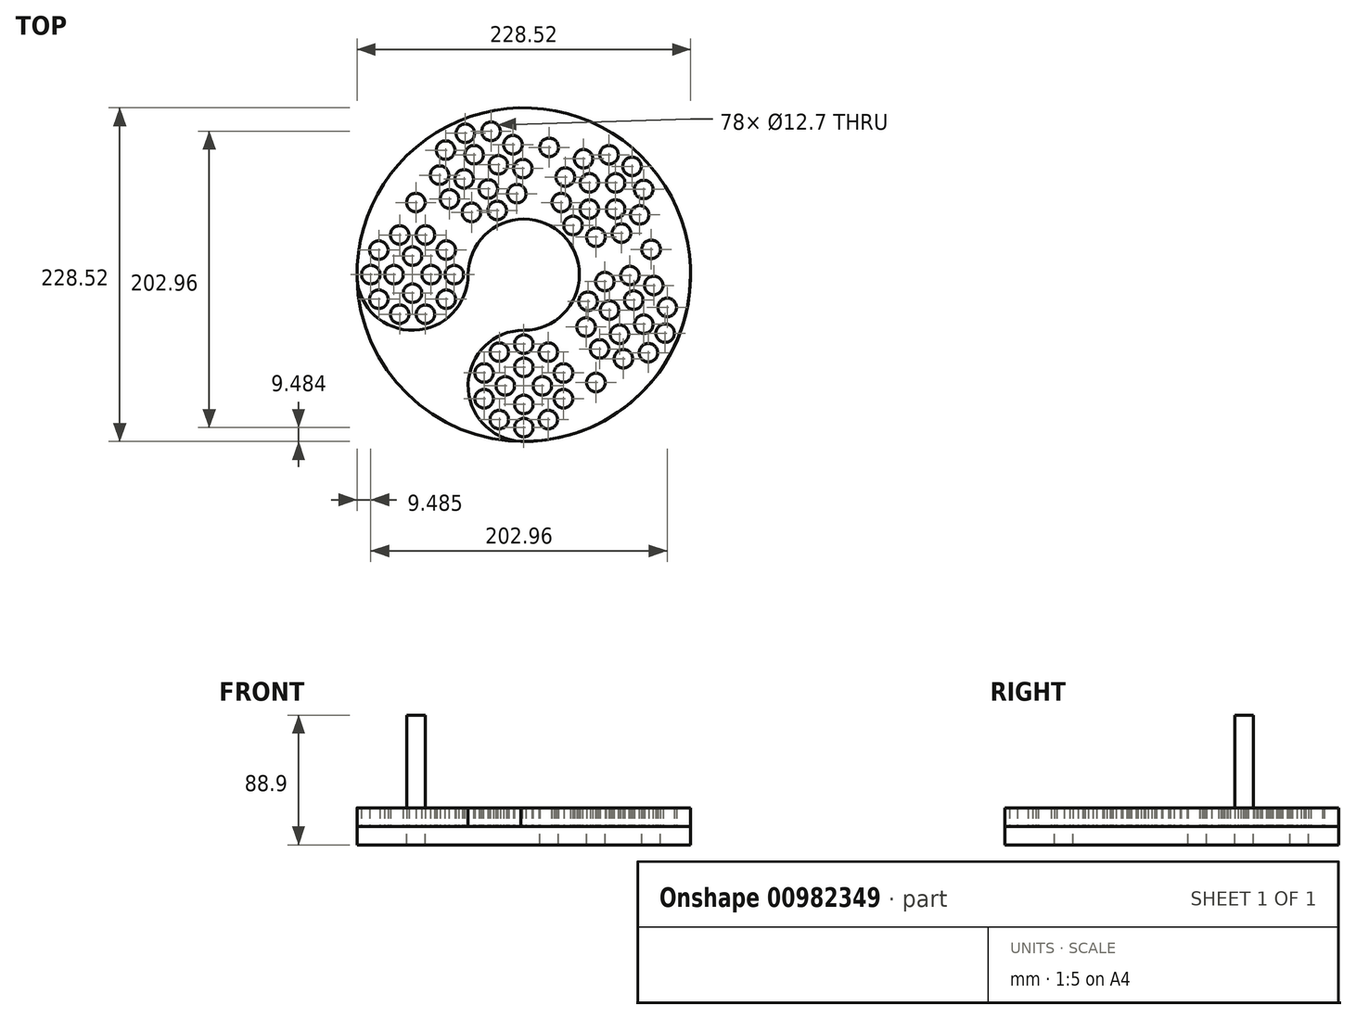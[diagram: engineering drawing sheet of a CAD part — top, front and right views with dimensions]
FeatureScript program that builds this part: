
annotation { "Feature Type Name" : "Feature", "Feature Type Description" : "" }
export const myFeature = defineFeature(function(context is Context, id is Id, definition is map)
    precondition{}
    {
        {
            var Q0;
            Q0=qCreatedBy(makeId("Top.planeOp"),FACE);
            var sketch = newSketch(context, id + "F0", { "sketchPlane" : qUnion([Q0])});
            skArc(sketch, "E0", {"start": v(-101.16, 18.78) * mm, "mid": v(-64.22, -21.5) * mm, "end": v(-25.02, 16.59) * mm});
            skCircle(sketch, "E1", {"center": v(13.08, 16.59) * mm, "radius": 38.1 * mm});
            skArc(sketch, "E2", {"start": v(-63.12, 16.59) * mm, "mid": v(66.96, 70.47) * mm, "end": v(13.08, -59.61) * mm, "construction": true});
            skArc(sketch, "E3", {"start": v(13.08, -21.51) * mm, "mid": v(-25, -60.7) * mm, "end": v(15.27, -97.65) * mm});
            skArc(sketch, "E4", {"start": v(-101.16, 14.4) * mm, "mid": v(92.3, 98.92) * mm, "end": v(15.27, -97.65) * mm});
            skCircle(sketch, "E5", {"center": v(13.08, 16.59) * mm, "radius": 114.26 * mm});
            skCircle(sketch, "E6", {"center": v(-50.42, 16.59) * mm, "radius": 6.35 * mm});
            skCircle(sketch, "E7", {"center": v(-34.55, 16.59) * mm, "radius": 6.35 * mm});
            skCircle(sketch, "E8.1.0", {"center": v(-63.12, 29.29) * mm, "radius": 6.35 * mm});
            skCircle(sketch, "E8.2.0", {"center": v(-75.82, 16.59) * mm, "radius": 6.35 * mm});
            skCircle(sketch, "E8.3.0", {"center": v(-63.12, 3.89) * mm, "radius": 6.35 * mm});
            skCircle(sketch, "E9.1.0", {"center": v(-40, 33.38) * mm, "radius": 6.35 * mm});
            skCircle(sketch, "E9.2.0", {"center": v(-54.3, 43.77) * mm, "radius": 6.35 * mm});
            skCircle(sketch, "E9.3.0", {"center": v(-71.95, 43.77) * mm, "radius": 6.35 * mm});
            skCircle(sketch, "E9.4.0", {"center": v(-86.24, 33.38) * mm, "radius": 6.35 * mm});
            skCircle(sketch, "E9.5.0", {"center": v(-91.7, 16.59) * mm, "radius": 6.35 * mm});
            skCircle(sketch, "E9.6.0", {"center": v(-86.24, -0.2) * mm, "radius": 6.35 * mm});
            skCircle(sketch, "E9.7.0", {"center": v(-71.95, -10.59) * mm, "radius": 6.35 * mm});
            skCircle(sketch, "E9.8.0", {"center": v(-54.3, -10.59) * mm, "radius": 6.35 * mm});
            skCircle(sketch, "E9.9.0", {"center": v(-40, -0.2) * mm, "radius": 6.35 * mm});
            skLineSegment(sketch, "E10", {"start": v(-63.12, 16.59) * mm, "end": v(13.08, 16.59) * mm, "construction": true});
            skLineSegment(sketch, "E11", {"start": v(13.08, 16.59) * mm, "end": v(13.08, -59.61) * mm, "construction": true});
            skCircle(sketch, "E12.1.0", {"center": v(5.65, 105.55) * mm, "radius": 6.35 * mm});
            skCircle(sketch, "E12.1.1", {"center": v(-9.41, 114.77) * mm, "radius": 6.35 * mm});
            skCircle(sketch, "E12.1.2", {"center": v(-27.02, 113.39) * mm, "radius": 6.35 * mm});
            skCircle(sketch, "E12.1.3", {"center": v(-20.94, 98.72) * mm, "radius": 6.35 * mm});
            skCircle(sketch, "E12.1.4", {"center": v(-40.45, 101.92) * mm, "radius": 6.35 * mm});
            skCircle(sketch, "E12.1.5", {"center": v(-44.57, 84.75) * mm, "radius": 6.35 * mm});
            skCircle(sketch, "E12.1.6", {"center": v(-27.81, 82.13) * mm, "radius": 6.35 * mm});
            skCircle(sketch, "E12.1.7", {"center": v(-37.8, 68.43) * mm, "radius": 6.35 * mm});
            skCircle(sketch, "E12.1.8", {"center": v(-22.75, 59.2) * mm, "radius": 6.35 * mm});
            skCircle(sketch, "E12.1.9", {"center": v(-5.15, 60.59) * mm, "radius": 6.35 * mm});
            skCircle(sketch, "E12.1.10", {"center": v(-11.22, 75.26) * mm, "radius": 6.35 * mm});
            skCircle(sketch, "E12.1.11", {"center": v(-4.35, 91.85) * mm, "radius": 6.35 * mm});
            skCircle(sketch, "E12.1.12", {"center": v(12.4, 89.23) * mm, "radius": 6.35 * mm});
            skCircle(sketch, "E12.1.13", {"center": v(8.28, 72.06) * mm, "radius": 6.35 * mm});
            skCircle(sketch, "E12.2.0", {"center": v(92.42, 57.5) * mm, "radius": 6.35 * mm});
            skCircle(sketch, "E12.2.1", {"center": v(95.18, 74.94) * mm, "radius": 6.35 * mm});
            skCircle(sketch, "E12.2.2", {"center": v(87.17, 90.68) * mm, "radius": 6.35 * mm});
            skCircle(sketch, "E12.2.3", {"center": v(75.94, 79.45) * mm, "radius": 6.35 * mm});
            skCircle(sketch, "E12.2.4", {"center": v(71.43, 98.7) * mm, "radius": 6.35 * mm});
            skCircle(sketch, "E12.2.5", {"center": v(53.99, 95.93) * mm, "radius": 6.35 * mm});
            skCircle(sketch, "E12.2.6", {"center": v(57.98, 79.45) * mm, "radius": 6.35 * mm});
            skCircle(sketch, "E12.2.7", {"center": v(41.5, 83.44) * mm, "radius": 6.35 * mm});
            skCircle(sketch, "E12.2.8", {"center": v(38.74, 66) * mm, "radius": 6.35 * mm});
            skCircle(sketch, "E12.2.9", {"center": v(46.76, 50.26) * mm, "radius": 6.35 * mm});
            skCircle(sketch, "E12.2.10", {"center": v(57.98, 61.5) * mm, "radius": 6.35 * mm});
            skCircle(sketch, "E12.2.11", {"center": v(75.94, 61.5) * mm, "radius": 6.35 * mm});
            skCircle(sketch, "E12.2.12", {"center": v(79.93, 45.01) * mm, "radius": 6.35 * mm});
            skCircle(sketch, "E12.2.13", {"center": v(62.5, 42.25) * mm, "radius": 6.35 * mm});
            skCircle(sketch, "E12.3.0", {"center": v(81.24, -41.06) * mm, "radius": 6.35 * mm});
            skCircle(sketch, "E12.3.1", {"center": v(98.4, -36.94) * mm, "radius": 6.35 * mm});
            skCircle(sketch, "E12.3.2", {"center": v(109.88, -23.5) * mm, "radius": 6.35 * mm});
            skCircle(sketch, "E12.3.3", {"center": v(95.21, -17.43) * mm, "radius": 6.35 * mm});
            skCircle(sketch, "E12.3.4", {"center": v(111.26, -5.9) * mm, "radius": 6.35 * mm});
            skCircle(sketch, "E12.3.5", {"center": v(102.04, 9.16) * mm, "radius": 6.35 * mm});
            skCircle(sketch, "E12.3.6", {"center": v(88.34, -0.84) * mm, "radius": 6.35 * mm});
            skCircle(sketch, "E12.3.7", {"center": v(85.72, 15.92) * mm, "radius": 6.35 * mm});
            skCircle(sketch, "E12.3.8", {"center": v(68.55, 11.8) * mm, "radius": 6.35 * mm});
            skCircle(sketch, "E12.3.9", {"center": v(57.08, -1.64) * mm, "radius": 6.35 * mm});
            skCircle(sketch, "E12.3.10", {"center": v(71.75, -7.71) * mm, "radius": 6.35 * mm});
            skCircle(sketch, "E12.3.11", {"center": v(78.62, -24.3) * mm, "radius": 6.35 * mm});
            skCircle(sketch, "E12.3.12", {"center": v(64.92, -34.3) * mm, "radius": 6.35 * mm});
            skCircle(sketch, "E12.3.13", {"center": v(55.7, -19.24) * mm, "radius": 6.35 * mm});
            skCircle(sketch, "E12.4.0", {"center": v(-14.1, -68.44) * mm, "radius": 6.35 * mm});
            skCircle(sketch, "E12.4.1", {"center": v(-3.72, -82.73) * mm, "radius": 6.35 * mm});
            skCircle(sketch, "E12.4.2", {"center": v(13.08, -88.19) * mm, "radius": 6.35 * mm});
            skCircle(sketch, "E12.4.3", {"center": v(13.08, -72.31) * mm, "radius": 6.35 * mm});
            skCircle(sketch, "E12.4.4", {"center": v(29.88, -82.73) * mm, "radius": 6.35 * mm});
            skCircle(sketch, "E12.4.5", {"center": v(40.26, -68.44) * mm, "radius": 6.35 * mm});
            skCircle(sketch, "E12.4.6", {"center": v(25.78, -59.61) * mm, "radius": 6.35 * mm});
            skCircle(sketch, "E12.4.7", {"center": v(40.26, -50.78) * mm, "radius": 6.35 * mm});
            skCircle(sketch, "E12.4.8", {"center": v(29.88, -36.5) * mm, "radius": 6.35 * mm});
            skCircle(sketch, "E12.4.9", {"center": v(13.08, -31.04) * mm, "radius": 6.35 * mm});
            skCircle(sketch, "E12.4.10", {"center": v(13.08, -46.91) * mm, "radius": 6.35 * mm});
            skCircle(sketch, "E12.4.11", {"center": v(0.38, -59.61) * mm, "radius": 6.35 * mm});
            skCircle(sketch, "E12.4.12", {"center": v(-14.1, -50.78) * mm, "radius": 6.35 * mm});
            skCircle(sketch, "E12.4.13", {"center": v(-3.72, -36.5) * mm, "radius": 6.35 * mm});
            skLineSegment(sketch, "E12.anchor1", {"start": v(13.08, 16.59) * mm, "end": v(-91.7, 16.59) * mm, "construction": true});
            skLineSegment(sketch, "E12.anchor2", {"start": v(13.08, 16.59) * mm, "end": v(13.08, -88.19) * mm, "construction": true});
            skCircle(sketch, "E13.1.0", {"center": v(-60.84, 65.98) * mm, "radius": 6.35 * mm});
            skCircle(sketch, "E13.3.0", {"center": v(30.42, 103.78) * mm, "radius": 6.35 * mm});
            skCircle(sketch, "E13.5.0", {"center": v(100.27, 33.93) * mm, "radius": 6.35 * mm});
            skCircle(sketch, "E13.7.0", {"center": v(62.47, -57.33) * mm, "radius": 6.35 * mm});
            skLineSegment(sketch, "E13.anchor1", {"start": v(13.08, 16.59) * mm, "end": v(-75.82, 16.59) * mm, "construction": true});
            skLineSegment(sketch, "E13.anchor2", {"start": v(13.08, 16.59) * mm, "end": v(13.08, -72.31) * mm, "construction": true});
            skSolve(sketch);
        }
        {
            var Q0;
            {var subQ0=sQuery(id+"F0.wireOp",EDGE,"E1");var subQ1=sQuery(id+"F0.wireOp",EDGE,"E0");var subQ2=makeQuery(id+"F0.imprint","INTERSECT",VERTEX,{"derivedFrom":[subQ1,subQ0]});Q0=makeQuery(id+"F0.imprint","IMPRINT",FACE,{"disambiguationData":[TD([[makeQuery(id+"F0.imprint","IMPRINT",EDGE,{"disambiguationData":[TD([[subQ2,1.0]])],"derivedFrom":subQ1}),-1.0]])]});}
            var Q1;
            {var subQ0=sQuery(id+"F0.wireOp",EDGE,"E1");var subQ1=makeQuery(id+"F0.imprint","INTERSECT",VERTEX,{"derivedFrom":[sQuery(id+"F0.wireOp",EDGE,"E0"),subQ0]});Q1=makeQuery(id+"F0.imprint","IMPRINT",FACE,{"disambiguationData":[TD([[makeQuery(id+"F0.imprint","IMPRINT",EDGE,{"disambiguationData":[TD([[subQ1,-1.0]])],"derivedFrom":subQ0}),1.0]])]});}
            var Q2;
            Q2=makeQuery(id+"F0.imprint","IMPRINT",FACE,{"disambiguationData":[TD([[makeQuery(id+"F0.imprint","IMPRINT",EDGE,{"derivedFrom":sQuery(id+"F0.wireOp",EDGE,"E6")}),-1.0]])]});
            var Q3;
            Q3=makeQuery(id+"F0.imprint","IMPRINT",FACE,{"disambiguationData":[TD([[makeQuery(id+"F0.imprint","IMPRINT",EDGE,{"derivedFrom":sQuery(id+"F0.wireOp",EDGE,"E9.4.0")}),1.0]])]});
            var Q4;
            Q4=makeQuery(id+"F0.imprint","IMPRINT",FACE,{"disambiguationData":[TD([[makeQuery(id+"F0.imprint","IMPRINT",EDGE,{"derivedFrom":sQuery(id+"F0.wireOp",EDGE,"E12.4.12")}),1.0]])]});
            var Q5;
            Q5=makeQuery(id+"F0.imprint","IMPRINT",FACE,{"disambiguationData":[TD([[makeQuery(id+"F0.imprint","IMPRINT",EDGE,{"derivedFrom":sQuery(id+"F0.wireOp",EDGE,"E12.4.10")}),1.0]])]});
            var Q6;
            Q6=makeQuery(id+"F0.imprint","IMPRINT",FACE,{"disambiguationData":[TD([[makeQuery(id+"F0.imprint","IMPRINT",EDGE,{"derivedFrom":sQuery(id+"F0.wireOp",EDGE,"E12.4.2")}),1.0]])]});
            var Q7;
            Q7=makeQuery(id+"F0.imprint","IMPRINT",FACE,{"disambiguationData":[TD([[makeQuery(id+"F0.imprint","IMPRINT",EDGE,{"derivedFrom":sQuery(id+"F0.wireOp",EDGE,"E9.3.0")}),1.0]])]});
            var Q8;
            Q8=makeQuery(id+"F0.imprint","IMPRINT",FACE,{"disambiguationData":[TD([[makeQuery(id+"F0.imprint","IMPRINT",EDGE,{"derivedFrom":sQuery(id+"F0.wireOp",EDGE,"E12.4.13")}),1.0]])]});
            var Q9;
            Q9=makeQuery(id+"F0.imprint","IMPRINT",FACE,{"disambiguationData":[TD([[makeQuery(id+"F0.imprint","IMPRINT",EDGE,{"derivedFrom":sQuery(id+"F0.wireOp",EDGE,"E12.4.8")}),1.0]])]});
            var Q10;
            Q10=makeQuery(id+"F0.imprint","IMPRINT",FACE,{"disambiguationData":[TD([[makeQuery(id+"F0.imprint","IMPRINT",EDGE,{"derivedFrom":sQuery(id+"F0.wireOp",EDGE,"E12.4.3")}),1.0]])]});
            var Q11;
            Q11=makeQuery(id+"F0.imprint","IMPRINT",FACE,{"disambiguationData":[TD([[makeQuery(id+"F0.imprint","IMPRINT",EDGE,{"derivedFrom":sQuery(id+"F0.wireOp",EDGE,"E12.3.12")}),1.0]])]});
            var Q12;
            Q12=makeQuery(id+"F0.imprint","IMPRINT",FACE,{"disambiguationData":[TD([[makeQuery(id+"F0.imprint","IMPRINT",EDGE,{"derivedFrom":sQuery(id+"F0.wireOp",EDGE,"E12.4.0")}),1.0]])]});
            var Q13;
            Q13=makeQuery(id+"F0.imprint","IMPRINT",FACE,{"disambiguationData":[TD([[makeQuery(id+"F0.imprint","IMPRINT",EDGE,{"derivedFrom":sQuery(id+"F0.wireOp",EDGE,"E12.4.1")}),1.0]])]});
            var Q14;
            Q14=makeQuery(id+"F0.imprint","IMPRINT",FACE,{"disambiguationData":[TD([[makeQuery(id+"F0.imprint","IMPRINT",EDGE,{"derivedFrom":sQuery(id+"F0.wireOp",EDGE,"E12.4.9")}),1.0]])]});
            var Q15;
            Q15=makeQuery(id+"F0.imprint","IMPRINT",FACE,{"disambiguationData":[TD([[makeQuery(id+"F0.imprint","IMPRINT",EDGE,{"derivedFrom":sQuery(id+"F0.wireOp",EDGE,"E12.3.10")}),1.0]])]});
            var Q16;
            Q16=makeQuery(id+"F0.imprint","IMPRINT",FACE,{"disambiguationData":[TD([[makeQuery(id+"F0.imprint","IMPRINT",EDGE,{"derivedFrom":sQuery(id+"F0.wireOp",EDGE,"E8.2.0")}),1.0]])]});
            var Q17;
            Q17=makeQuery(id+"F0.imprint","IMPRINT",FACE,{"disambiguationData":[TD([[makeQuery(id+"F0.imprint","IMPRINT",EDGE,{"derivedFrom":sQuery(id+"F0.wireOp",EDGE,"E12.4.5")}),1.0]])]});
            var Q18;
            Q18=makeQuery(id+"F0.imprint","IMPRINT",FACE,{"disambiguationData":[TD([[makeQuery(id+"F0.imprint","IMPRINT",EDGE,{"derivedFrom":sQuery(id+"F0.wireOp",EDGE,"E12.3.4")}),1.0]])]});
            var Q19;
            Q19=makeQuery(id+"F0.imprint","IMPRINT",FACE,{"disambiguationData":[TD([[makeQuery(id+"F0.imprint","IMPRINT",EDGE,{"derivedFrom":sQuery(id+"F0.wireOp",EDGE,"E12.3.13")}),1.0]])]});
            var Q20;
            Q20=makeQuery(id+"F0.imprint","IMPRINT",FACE,{"disambiguationData":[TD([[makeQuery(id+"F0.imprint","IMPRINT",EDGE,{"derivedFrom":sQuery(id+"F0.wireOp",EDGE,"E9.6.0")}),1.0]])]});
            var Q21;
            Q21=makeQuery(id+"F0.imprint","IMPRINT",FACE,{"disambiguationData":[TD([[makeQuery(id+"F0.imprint","IMPRINT",EDGE,{"derivedFrom":sQuery(id+"F0.wireOp",EDGE,"E12.3.7")}),1.0]])]});
            var Q22;
            Q22=makeQuery(id+"F0.imprint","IMPRINT",FACE,{"disambiguationData":[TD([[makeQuery(id+"F0.imprint","IMPRINT",EDGE,{"derivedFrom":sQuery(id+"F0.wireOp",EDGE,"E9.9.0")}),1.0]])]});
            var Q23;
            Q23=makeQuery(id+"F0.imprint","IMPRINT",FACE,{"disambiguationData":[TD([[makeQuery(id+"F0.imprint","IMPRINT",EDGE,{"derivedFrom":sQuery(id+"F0.wireOp",EDGE,"E12.3.3")}),1.0]])]});
            var Q24;
            Q24=makeQuery(id+"F0.imprint","IMPRINT",FACE,{"disambiguationData":[TD([[makeQuery(id+"F0.imprint","IMPRINT",EDGE,{"derivedFrom":sQuery(id+"F0.wireOp",EDGE,"E12.3.2")}),1.0]])]});
            var Q25;
            Q25=makeQuery(id+"F0.imprint","IMPRINT",FACE,{"disambiguationData":[TD([[makeQuery(id+"F0.imprint","IMPRINT",EDGE,{"derivedFrom":sQuery(id+"F0.wireOp",EDGE,"E12.3.1")}),1.0]])]});
            var Q26;
            Q26=makeQuery(id+"F0.imprint","IMPRINT",FACE,{"disambiguationData":[TD([[makeQuery(id+"F0.imprint","IMPRINT",EDGE,{"derivedFrom":sQuery(id+"F0.wireOp",EDGE,"E9.5.0")}),1.0]])]});
            var Q27;
            Q27=makeQuery(id+"F0.imprint","IMPRINT",FACE,{"disambiguationData":[TD([[makeQuery(id+"F0.imprint","IMPRINT",EDGE,{"derivedFrom":sQuery(id+"F0.wireOp",EDGE,"E12.4.4")}),1.0]])]});
            var Q28;
            Q28=makeQuery(id+"F0.imprint","IMPRINT",FACE,{"disambiguationData":[TD([[makeQuery(id+"F0.imprint","IMPRINT",EDGE,{"derivedFrom":sQuery(id+"F0.wireOp",EDGE,"E12.3.0")}),1.0]])]});
            var Q29;
            Q29=makeQuery(id+"F0.imprint","IMPRINT",FACE,{"disambiguationData":[TD([[makeQuery(id+"F0.imprint","IMPRINT",EDGE,{"derivedFrom":sQuery(id+"F0.wireOp",EDGE,"E12.4.11")}),1.0]])]});
            var Q30;
            Q30=makeQuery(id+"F0.imprint","IMPRINT",FACE,{"disambiguationData":[TD([[makeQuery(id+"F0.imprint","IMPRINT",EDGE,{"derivedFrom":sQuery(id+"F0.wireOp",EDGE,"E12.2.0")}),1.0]])]});
            var Q31;
            Q31=makeQuery(id+"F0.imprint","IMPRINT",FACE,{"disambiguationData":[TD([[makeQuery(id+"F0.imprint","IMPRINT",EDGE,{"derivedFrom":sQuery(id+"F0.wireOp",EDGE,"E12.2.1")}),1.0]])]});
            var Q32;
            Q32=makeQuery(id+"F0.imprint","IMPRINT",FACE,{"disambiguationData":[TD([[makeQuery(id+"F0.imprint","IMPRINT",EDGE,{"derivedFrom":sQuery(id+"F0.wireOp",EDGE,"E8.3.0")}),1.0]])]});
            var Q33;
            Q33=makeQuery(id+"F0.imprint","IMPRINT",FACE,{"disambiguationData":[TD([[makeQuery(id+"F0.imprint","IMPRINT",EDGE,{"derivedFrom":sQuery(id+"F0.wireOp",EDGE,"E12.3.9")}),1.0]])]});
            var Q34;
            Q34=makeQuery(id+"F0.imprint","IMPRINT",FACE,{"disambiguationData":[TD([[makeQuery(id+"F0.imprint","IMPRINT",EDGE,{"derivedFrom":sQuery(id+"F0.wireOp",EDGE,"E12.3.5")}),1.0]])]});
            var Q35;
            {var subQ0=sQuery(id+"F0.wireOp",EDGE,"E5");var subQ1=sQuery(id+"F0.wireOp",EDGE,"E3");var subQ2=makeQuery(id+"F0.imprint","INTERSECT",VERTEX,{"disambiguationData":[OD(0.0)],"derivedFrom":[subQ1,subQ0]});Q35=makeQuery(id+"F0.imprint","IMPRINT",FACE,{"disambiguationData":[TD([[makeQuery(id+"F0.imprint","IMPRINT",EDGE,{"disambiguationData":[TD([[subQ2,1.0]])],"derivedFrom":subQ1}),1.0]])]});}
            var Q36;
            Q36=makeQuery(id+"F0.imprint","IMPRINT",FACE,{"disambiguationData":[TD([[makeQuery(id+"F0.imprint","IMPRINT",EDGE,{"derivedFrom":sQuery(id+"F0.wireOp",EDGE,"E12.4.6")}),1.0]])]});
            var Q37;
            Q37=makeQuery(id+"F0.imprint","IMPRINT",FACE,{"disambiguationData":[TD([[makeQuery(id+"F0.imprint","IMPRINT",EDGE,{"derivedFrom":sQuery(id+"F0.wireOp",EDGE,"E12.3.11")}),1.0]])]});
            var Q38;
            Q38=makeQuery(id+"F0.imprint","IMPRINT",FACE,{"disambiguationData":[TD([[makeQuery(id+"F0.imprint","IMPRINT",EDGE,{"derivedFrom":sQuery(id+"F0.wireOp",EDGE,"E12.3.6")}),1.0]])]});
            var Q39;
            Q39=makeQuery(id+"F0.imprint","IMPRINT",FACE,{"disambiguationData":[TD([[makeQuery(id+"F0.imprint","IMPRINT",EDGE,{"derivedFrom":sQuery(id+"F0.wireOp",EDGE,"E9.7.0")}),1.0]])]});
            var Q40;
            Q40=makeQuery(id+"F0.imprint","IMPRINT",FACE,{"disambiguationData":[TD([[makeQuery(id+"F0.imprint","IMPRINT",EDGE,{"derivedFrom":sQuery(id+"F0.wireOp",EDGE,"E12.4.7")}),1.0]])]});
            var Q41;
            Q41=makeQuery(id+"F0.imprint","IMPRINT",FACE,{"disambiguationData":[TD([[makeQuery(id+"F0.imprint","IMPRINT",EDGE,{"derivedFrom":sQuery(id+"F0.wireOp",EDGE,"E9.8.0")}),1.0]])]});
            var Q42;
            Q42=makeQuery(id+"F0.imprint","IMPRINT",FACE,{"disambiguationData":[TD([[makeQuery(id+"F0.imprint","IMPRINT",EDGE,{"derivedFrom":sQuery(id+"F0.wireOp",EDGE,"E12.2.12")}),1.0]])]});
            var Q43;
            Q43=makeQuery(id+"F0.imprint","IMPRINT",FACE,{"disambiguationData":[TD([[makeQuery(id+"F0.imprint","IMPRINT",EDGE,{"derivedFrom":sQuery(id+"F0.wireOp",EDGE,"E12.1.4")}),1.0]])]});
            var Q44;
            Q44=makeQuery(id+"F0.imprint","IMPRINT",FACE,{"disambiguationData":[TD([[makeQuery(id+"F0.imprint","IMPRINT",EDGE,{"derivedFrom":sQuery(id+"F0.wireOp",EDGE,"E12.2.3")}),1.0]])]});
            var Q45;
            Q45=makeQuery(id+"F0.imprint","IMPRINT",FACE,{"disambiguationData":[TD([[makeQuery(id+"F0.imprint","IMPRINT",EDGE,{"derivedFrom":sQuery(id+"F0.wireOp",EDGE,"E12.2.5")}),1.0]])]});
            var Q46;
            Q46=makeQuery(id+"F0.imprint","IMPRINT",FACE,{"disambiguationData":[TD([[makeQuery(id+"F0.imprint","IMPRINT",EDGE,{"derivedFrom":sQuery(id+"F0.wireOp",EDGE,"E6")}),1.0]])]});
            var Q47;
            Q47=makeQuery(id+"F0.imprint","IMPRINT",FACE,{"disambiguationData":[TD([[makeQuery(id+"F0.imprint","IMPRINT",EDGE,{"derivedFrom":sQuery(id+"F0.wireOp",EDGE,"E12.1.9")}),1.0]])]});
            var Q48;
            Q48=makeQuery(id+"F0.imprint","IMPRINT",FACE,{"disambiguationData":[TD([[makeQuery(id+"F0.imprint","IMPRINT",EDGE,{"derivedFrom":sQuery(id+"F0.wireOp",EDGE,"E12.2.4")}),1.0]])]});
            var Q49;
            {var subQ0=sQuery(id+"F0.wireOp",EDGE,"E5");var subQ1=sQuery(id+"F0.wireOp",EDGE,"E0");var subQ2=makeQuery(id+"F0.imprint","INTERSECT",VERTEX,{"disambiguationData":[OD(0.0)],"derivedFrom":[subQ1,subQ0]});Q49=makeQuery(id+"F0.imprint","IMPRINT",FACE,{"disambiguationData":[TD([[makeQuery(id+"F0.imprint","IMPRINT",EDGE,{"disambiguationData":[TD([[subQ2,-1.0]])],"derivedFrom":subQ1}),1.0]])]});}
            var Q50;
            Q50=makeQuery(id+"F0.imprint","IMPRINT",FACE,{"disambiguationData":[TD([[makeQuery(id+"F0.imprint","IMPRINT",EDGE,{"derivedFrom":sQuery(id+"F0.wireOp",EDGE,"E9.2.0")}),1.0]])]});
            var Q51;
            Q51=makeQuery(id+"F0.imprint","IMPRINT",FACE,{"disambiguationData":[TD([[makeQuery(id+"F0.imprint","IMPRINT",EDGE,{"derivedFrom":sQuery(id+"F0.wireOp",EDGE,"E12.1.10")}),1.0]])]});
            var Q52;
            Q52=makeQuery(id+"F0.imprint","IMPRINT",FACE,{"disambiguationData":[TD([[makeQuery(id+"F0.imprint","IMPRINT",EDGE,{"derivedFrom":sQuery(id+"F0.wireOp",EDGE,"E12.2.6")}),1.0]])]});
            var Q53;
            Q53=makeQuery(id+"F0.imprint","IMPRINT",FACE,{"disambiguationData":[TD([[makeQuery(id+"F0.imprint","IMPRINT",EDGE,{"derivedFrom":sQuery(id+"F0.wireOp",EDGE,"E12.1.0")}),1.0]])]});
            var Q54;
            Q54=makeQuery(id+"F0.imprint","IMPRINT",FACE,{"disambiguationData":[TD([[makeQuery(id+"F0.imprint","IMPRINT",EDGE,{"derivedFrom":sQuery(id+"F0.wireOp",EDGE,"E12.1.13")}),1.0]])]});
            var Q55;
            Q55=makeQuery(id+"F0.imprint","IMPRINT",FACE,{"disambiguationData":[TD([[makeQuery(id+"F0.imprint","IMPRINT",EDGE,{"derivedFrom":sQuery(id+"F0.wireOp",EDGE,"E12.1.11")}),1.0]])]});
            var Q56;
            Q56=makeQuery(id+"F0.imprint","IMPRINT",FACE,{"disambiguationData":[TD([[makeQuery(id+"F0.imprint","IMPRINT",EDGE,{"derivedFrom":sQuery(id+"F0.wireOp",EDGE,"E12.1.12")}),1.0]])]});
            var Q57;
            Q57=makeQuery(id+"F0.imprint","IMPRINT",FACE,{"disambiguationData":[TD([[makeQuery(id+"F0.imprint","IMPRINT",EDGE,{"derivedFrom":sQuery(id+"F0.wireOp",EDGE,"E12.2.10")}),1.0]])]});
            var Q58;
            Q58=makeQuery(id+"F0.imprint","IMPRINT",FACE,{"disambiguationData":[TD([[makeQuery(id+"F0.imprint","IMPRINT",EDGE,{"derivedFrom":sQuery(id+"F0.wireOp",EDGE,"E12.1.3")}),1.0]])]});
            var Q59;
            Q59=makeQuery(id+"F0.imprint","IMPRINT",FACE,{"disambiguationData":[TD([[makeQuery(id+"F0.imprint","IMPRINT",EDGE,{"derivedFrom":sQuery(id+"F0.wireOp",EDGE,"E7")}),1.0]])]});
            var Q60;
            Q60=makeQuery(id+"F0.imprint","IMPRINT",FACE,{"disambiguationData":[TD([[makeQuery(id+"F0.imprint","IMPRINT",EDGE,{"derivedFrom":sQuery(id+"F0.wireOp",EDGE,"E12.1.5")}),1.0]])]});
            var Q61;
            Q61=makeQuery(id+"F0.imprint","IMPRINT",FACE,{"disambiguationData":[TD([[makeQuery(id+"F0.imprint","IMPRINT",EDGE,{"derivedFrom":sQuery(id+"F0.wireOp",EDGE,"E12.2.11")}),1.0]])]});
            var Q62;
            Q62=makeQuery(id+"F0.imprint","IMPRINT",FACE,{"disambiguationData":[TD([[makeQuery(id+"F0.imprint","IMPRINT",EDGE,{"derivedFrom":sQuery(id+"F0.wireOp",EDGE,"E12.1.7")}),1.0]])]});
            var Q63;
            Q63=makeQuery(id+"F0.imprint","IMPRINT",FACE,{"disambiguationData":[TD([[makeQuery(id+"F0.imprint","IMPRINT",EDGE,{"derivedFrom":sQuery(id+"F0.wireOp",EDGE,"E12.2.9")}),1.0]])]});
            var Q64;
            Q64=makeQuery(id+"F0.imprint","IMPRINT",FACE,{"disambiguationData":[TD([[makeQuery(id+"F0.imprint","IMPRINT",EDGE,{"derivedFrom":sQuery(id+"F0.wireOp",EDGE,"E12.2.13")}),1.0]])]});
            var Q65;
            Q65=makeQuery(id+"F0.imprint","IMPRINT",FACE,{"disambiguationData":[TD([[makeQuery(id+"F0.imprint","IMPRINT",EDGE,{"derivedFrom":sQuery(id+"F0.wireOp",EDGE,"E12.1.8")}),1.0]])]});
            var Q66;
            Q66=makeQuery(id+"F0.imprint","IMPRINT",FACE,{"disambiguationData":[TD([[makeQuery(id+"F0.imprint","IMPRINT",EDGE,{"derivedFrom":sQuery(id+"F0.wireOp",EDGE,"E8.1.0")}),1.0]])]});
            var Q67;
            Q67=makeQuery(id+"F0.imprint","IMPRINT",FACE,{"disambiguationData":[TD([[makeQuery(id+"F0.imprint","IMPRINT",EDGE,{"derivedFrom":sQuery(id+"F0.wireOp",EDGE,"E12.1.2")}),1.0]])]});
            var Q68;
            Q68=makeQuery(id+"F0.imprint","IMPRINT",FACE,{"disambiguationData":[TD([[makeQuery(id+"F0.imprint","IMPRINT",EDGE,{"derivedFrom":sQuery(id+"F0.wireOp",EDGE,"E12.2.8")}),1.0]])]});
            var Q69;
            Q69=makeQuery(id+"F0.imprint","IMPRINT",FACE,{"disambiguationData":[TD([[makeQuery(id+"F0.imprint","IMPRINT",EDGE,{"derivedFrom":sQuery(id+"F0.wireOp",EDGE,"E12.2.2")}),1.0]])]});
            var Q70;
            Q70=makeQuery(id+"F0.imprint","IMPRINT",FACE,{"disambiguationData":[TD([[makeQuery(id+"F0.imprint","IMPRINT",EDGE,{"derivedFrom":sQuery(id+"F0.wireOp",EDGE,"E12.3.8")}),1.0]])]});
            var Q71;
            Q71=makeQuery(id+"F0.imprint","IMPRINT",FACE,{"disambiguationData":[TD([[makeQuery(id+"F0.imprint","IMPRINT",EDGE,{"derivedFrom":sQuery(id+"F0.wireOp",EDGE,"E12.1.1")}),1.0]])]});
            var Q72;
            Q72=makeQuery(id+"F0.imprint","IMPRINT",FACE,{"disambiguationData":[TD([[makeQuery(id+"F0.imprint","IMPRINT",EDGE,{"derivedFrom":sQuery(id+"F0.wireOp",EDGE,"E12.1.6")}),1.0]])]});
            var Q73;
            Q73=makeQuery(id+"F0.imprint","IMPRINT",FACE,{"disambiguationData":[TD([[makeQuery(id+"F0.imprint","IMPRINT",EDGE,{"derivedFrom":sQuery(id+"F0.wireOp",EDGE,"E9.1.0")}),1.0]])]});
            var Q74;
            Q74=makeQuery(id+"F0.imprint","IMPRINT",FACE,{"disambiguationData":[TD([[makeQuery(id+"F0.imprint","IMPRINT",EDGE,{"derivedFrom":sQuery(id+"F0.wireOp",EDGE,"E12.2.7")}),1.0]])]});
            extrude(context, id + "F1", {"entities" : qUnion([Q0, Q1, Q2, Q3, Q4, Q5, Q6, Q7, Q8, Q9, Q10, Q11, Q12, Q13, Q14, Q15, Q16, Q17, Q18, Q19, Q20, Q21, Q22, Q23, Q24, Q25, Q26, Q27, Q28, Q29, Q30, Q31, Q32, Q33, Q34, Q35, Q36, Q37, Q38, Q39, Q40, Q41, Q42, Q43, Q44, Q45, Q46, Q47, Q48, Q49, Q50, Q51, Q52, Q53, Q54, Q55, Q56, Q57, Q58, Q59, Q60, Q61, Q62, Q63, Q64, Q65, Q66, Q67, Q68, Q69, Q70, Q71, Q72, Q73, Q74]), "oppositeDirection" : true, "depth" : 12.7 * mm, "offsetDistance" : 25.4 * mm});
        }
        {
            var Q0;
            Q0=makeQuery(id+"F0.imprint","IMPRINT",FACE,{"disambiguationData":[TD([[makeQuery(id+"F0.imprint","IMPRINT",EDGE,{"derivedFrom":sQuery(id+"F0.wireOp",EDGE,"E6")}),-1.0]])]});
            extrude(context, id + "F2", {"entities" : qUnion([Q0]), "depth" : 12.7 * mm, "offsetDistance" : 25.4 * mm});
        }
        {
            var Q0;
            Q0=makeQuery(id+"F0.imprint","IMPRINT",FACE,{"disambiguationData":[TD([[makeQuery(id+"F0.imprint","IMPRINT",EDGE,{"derivedFrom":sQuery(id+"F0.wireOp",EDGE,"E13.1.0")}),1.0]])]});
            extrude(context, id + "F3", {"entities" : qUnion([Q0]), "depth" : 76.2 * mm, "offsetDistance" : 25.4 * mm});
        }
    });
